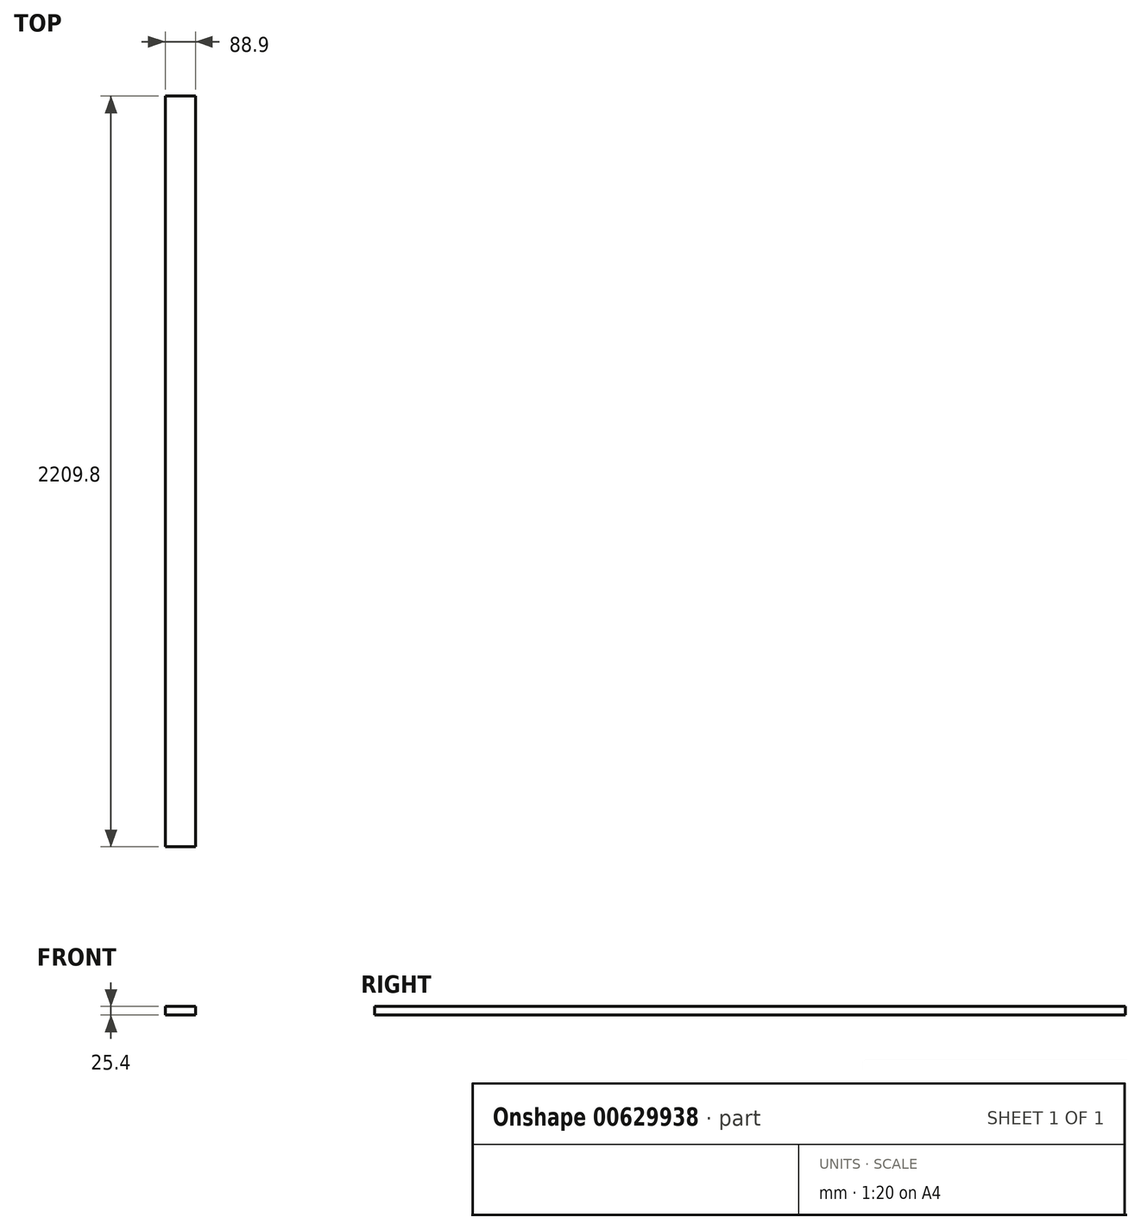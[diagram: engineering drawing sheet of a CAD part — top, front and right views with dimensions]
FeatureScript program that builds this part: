
annotation { "Feature Type Name" : "Feature", "Feature Type Description" : "" }
export const myFeature = defineFeature(function(context is Context, id is Id, definition is map)
    precondition{}
    {
        {
            var Q0;
            Q0=qCreatedBy(makeId("Front.planeOp"),FACE);
            var sketch = newSketch(context, id + "F0", { "sketchPlane" : qUnion([Q0])});
            skLineSegment(sketch, "E0.bottom", {"start": v(-39.65, 4.5) * mm, "end": v(49.25, 4.5) * mm});
            skLineSegment(sketch, "E0.top", {"start": v(-39.65, -20.9) * mm, "end": v(49.25, -20.9) * mm});
            skLineSegment(sketch, "E0.left", {"start": v(-39.65, 4.5) * mm, "end": v(-39.65, -20.9) * mm});
            skLineSegment(sketch, "E0.right", {"start": v(49.25, 4.5) * mm, "end": v(49.25, -20.9) * mm});
            skSolve(sketch);
        }
        {
            var Q0;
            Q0 = qSketchRegion(id + "F0", true);
            extrude(context, id + "F1", {"entities" : qUnion([Q0]), "depth" : 2209.8 * mm, "offsetDistance" : 25.4 * mm});
        }
    });
